# Revit family: IEK_Выключатель_ОткрытойУстановки_С Инд 10А одноклавишный IP54_ФОРС
name_source: partatom
category: Выключатели
units: mm (PartAtom-declared; Revit-internal decimal feet)

## family parameters
Всегда вертикально = Да
На основе рабочей плоскости = Нет
Общий = Нет
При загрузке вырезать с полостями = Нет
Размер круглого соединителя = Использовать диаметр
Сохранять ориентацию аннотаций = Да
Тип детали = Переключатель
Точка расчета площади = Нет

## types (1)
- ВС20-1-1-ФСр
    ADSK_URL страницы изделия = https://www.iek.ru
    ADSK_Версия Revit = 2019
    ADSK_Версия семейства = 1.0
    ADSK_Группирование = III ЭЛЕКТРОУСТАНОВОЧНЫЕ И ЭЛЕКТРОМОНТАЖНЫЕ ИЗДЕЛИЯ
    ADSK_Единица измерения = шт
    ADSK_Завод-изготовитель = IEK
    ADSK_Код изделия = EVS11-K03-10-54-DC
    ADSK_Количество фаз = 1
    ADSK_Количество фаз числовое = 1
    ADSK_Марка = ФОРС
    ADSK_Масса = 0.09
    ADSK_Материал = Окраска - RAL 7035
    ADSK_Материал наименование = Пластик
    ADSK_Наименование = Выключатель 1-клавишный для открытой установки с индикацией ВС20-1-1-ФСр ФОРС IP54 IEK
    ADSK_Напряжение = 220 В
    IEK_URL = https://www.iek.ru
    IEK_Описание = Выключатели и розетки серии «ФОРС» IP54 для открытой установки предназначены для помещений с повышенной влажностью и запыленностью: подвалов, гаражей, мастерских. Дизайн розеток и выключателей данной серии идеально впишется в интерьер промышленных предприятий.
    IEK_Цена за единицу = 429.28
    KSI_CMa_Строительные материалы = 01.7.14.03
    KSI_CPr_Строительные изделия = 20.4.01
    Высота = 92 мм
    Глубина = 55 мм
    Изготовитель = IEK
    Материал крышки = RAL 9004
    Степень защиты = IP54
    Тип монтажа = Поверхность монтажа (открытая установка)
    Ширина = 65 мм
